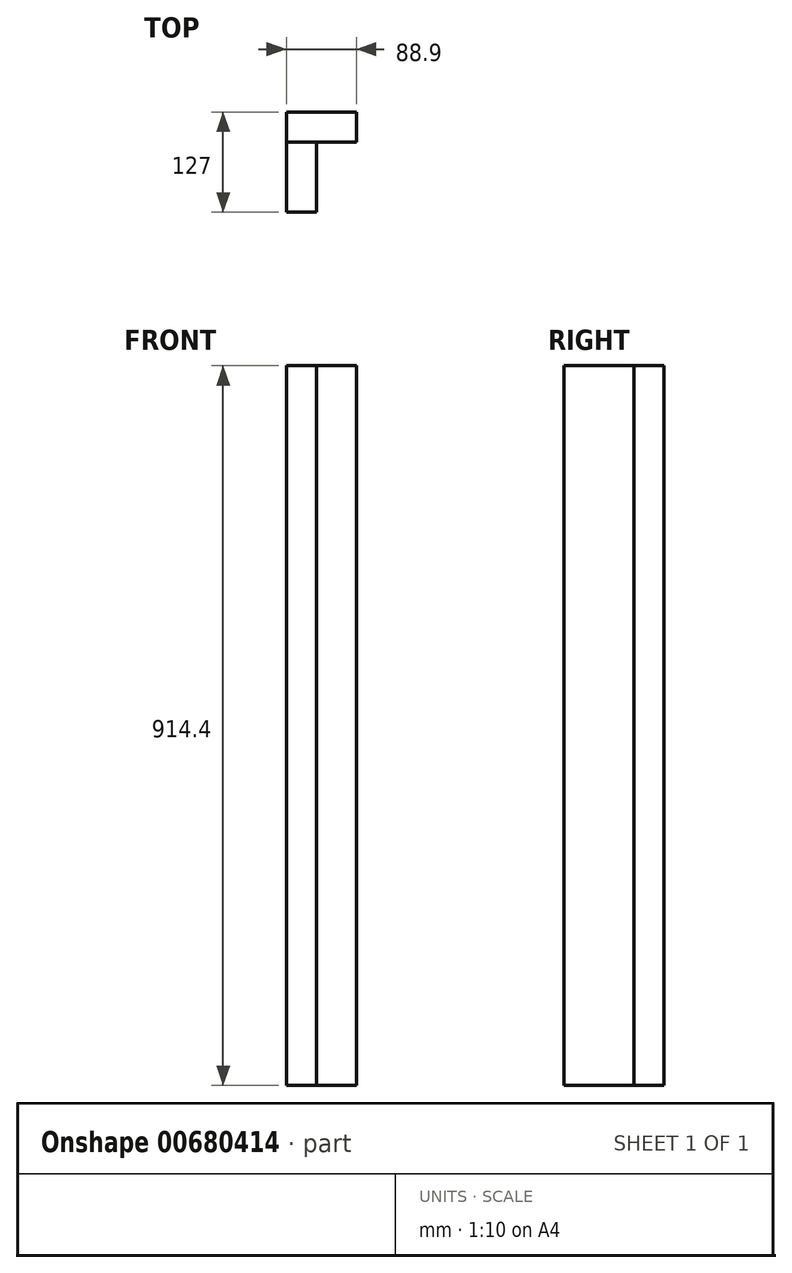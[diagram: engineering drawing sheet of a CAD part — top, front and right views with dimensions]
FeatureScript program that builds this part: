
annotation { "Feature Type Name" : "Feature", "Feature Type Description" : "" }
export const myFeature = defineFeature(function(context is Context, id is Id, definition is map)
    precondition{}
    {
        {
            var Q0;
            Q0=qCreatedBy(makeId("Top.planeOp"),FACE);
            var sketch = newSketch(context, id + "F0", { "sketchPlane" : qUnion([Q0])});
            skLineSegment(sketch, "E0.bottom", {"start": v(0, 0) * mm, "end": v(88.9, 0) * mm});
            skLineSegment(sketch, "E0.top", {"start": v(0, 38.1) * mm, "end": v(88.9, 38.1) * mm});
            skLineSegment(sketch, "E0.left", {"start": v(0, 0) * mm, "end": v(0, 38.1) * mm});
            skLineSegment(sketch, "E0.right", {"start": v(88.9, 0) * mm, "end": v(88.9, 38.1) * mm});
            skSolve(sketch);
        }
        {
            var Q0;
            Q0=makeQuery(id+"F0.imprint","IMPRINT",FACE,{"disambiguationData":[TD([[makeQuery(id+"F0.imprint","IMPRINT",EDGE,{"derivedFrom":sQuery(id+"F0.wireOp",EDGE,"E0.bottom")}),1.0]])]});
            extrude(context, id + "F1", {"entities" : qUnion([Q0]), "depth" : 914.4 * mm, "offsetDistance" : 25.4 * mm});
        }
        {
            var Q0;
            Q0=makeQuery(id+"F1.opExtrude","SWEPT_BODY",BODY,{"disambiguationData":[OSD([sQuery(id+"F0.wireOp",EDGE,"E0.bottom"),sQuery(id+"F0.wireOp",EDGE,"E0.top"),sQuery(id+"F0.wireOp",EDGE,"E0.left"),sQuery(id+"F0.wireOp",EDGE,"E0.right")])]});
            var Q1;
            Q1=makeQuery(id+"F1.opExtrude","SWEPT_EDGE",EDGE,{"disambiguationData":[OSD([sQuery(id+"F0.wireOp",EDGE,"E0.bottom"),sQuery(id+"F0.wireOp",EDGE,"E0.left")])]});
            transform(context, id + "F2", {"entities" : qUnion([Q0]), "transformType" : TransformType.ROTATION, "transformAxis" : qUnion([Q1]), "angle" : 90 * degree, "makeCopy" : true});
        }
    });
